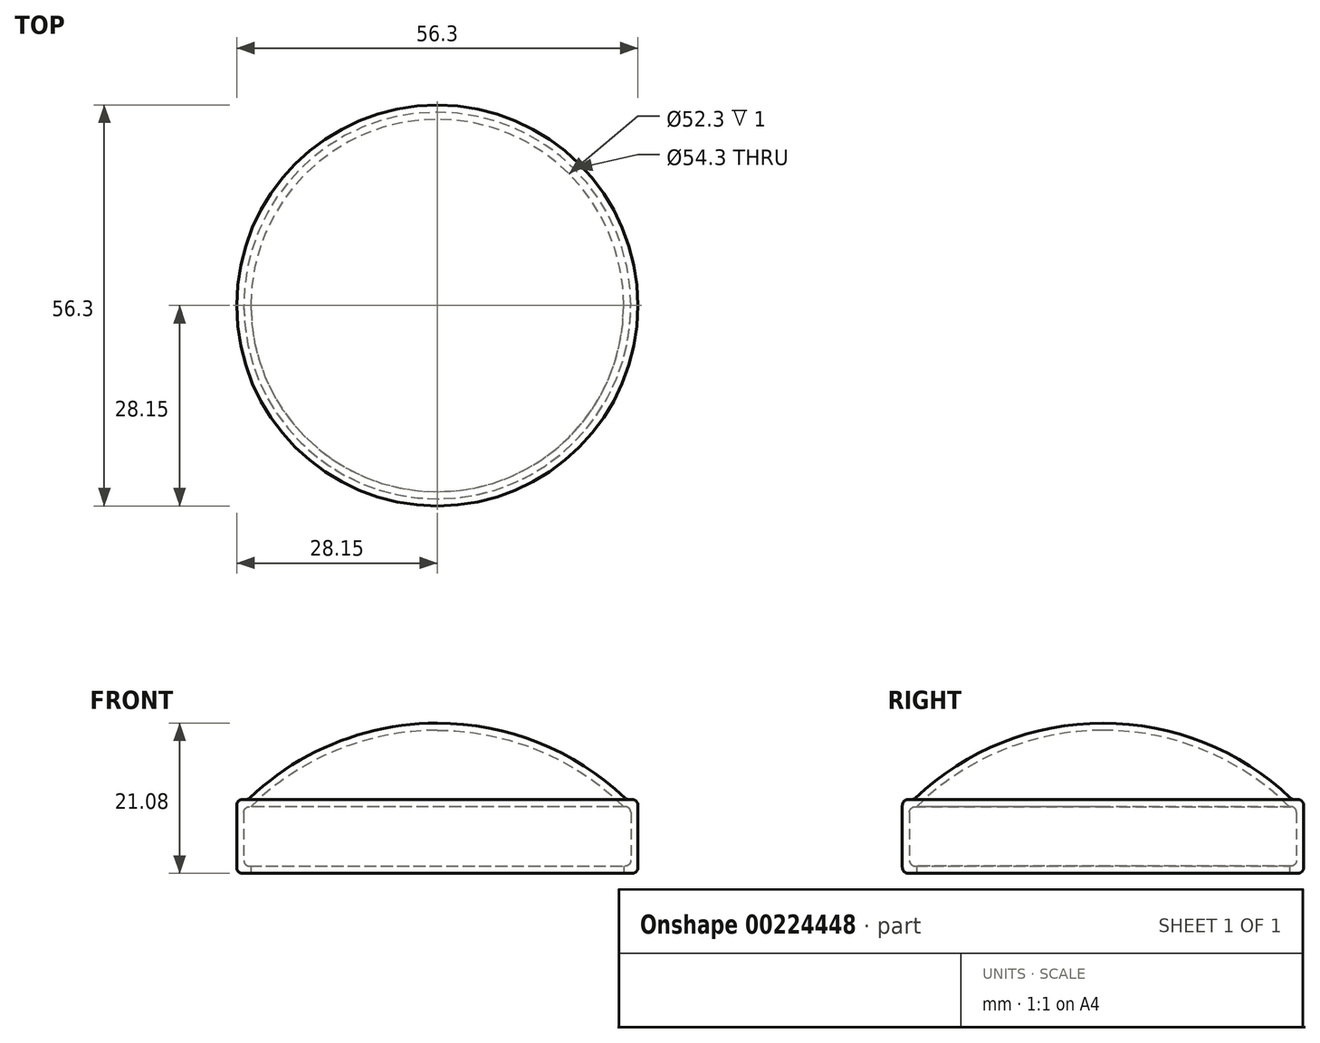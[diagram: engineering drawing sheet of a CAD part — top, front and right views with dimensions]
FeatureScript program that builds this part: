
annotation { "Feature Type Name" : "Feature", "Feature Type Description" : "" }
export const myFeature = defineFeature(function(context is Context, id is Id, definition is map)
    precondition{}
    {
        {
            assignVariable(context, id + "F0", {"name" : "WallThickness", "anyValue" : 1});
        }
        {
            var Q0;
            Q0=qCreatedBy(makeId("Front.planeOp"),FACE);
            var sketch = newSketch(context, id + "F1", { "sketchPlane" : qUnion([Q0])});
            skLineSegment(sketch, "E0", {"start": v(0, 0) * mm, "end": v(0, 27.56) * mm});
            skLineSegment(sketch, "E1", {"start": v(-26.15, 0) * mm, "end": v(-28.15, 0) * mm});
            skLineSegment(sketch, "E2", {"start": v(-28.15, 0) * mm, "end": v(-28.15, 10.35) * mm});
            skLineSegment(sketch, "E3", {"start": v(-28.15, 10.35) * mm, "end": v(-26.56, 10.35) * mm});
            skLineSegment(sketch, "E4", {"start": v(-26.15, 1) * mm, "end": v(-27.15, 1) * mm});
            skLineSegment(sketch, "E5", {"start": v(-27.15, 1) * mm, "end": v(-27.15, 9.35) * mm});
            skLineSegment(sketch, "E6", {"start": v(-27.15, 9.35) * mm, "end": v(-26.15, 9.35) * mm});
            skLineSegment(sketch, "E7", {"start": v(-26.15, 0) * mm, "end": v(-26.15, 1) * mm});
            skArc(sketch, "E8", {"start": v(0, 21.08) * mm, "mid": v(-14.32, 18.3) * mm, "end": v(-26.56, 10.35) * mm});
            skArc(sketch, "E9.0", {"start": v(0, 20.08) * mm, "mid": v(-14.13, 17.3) * mm, "end": v(-26.15, 9.35) * mm});
            skSolve(sketch);
        }
        {
            var Q0;
            Q0=makeQuery(id+"F1.imprint","IMPRINT",FACE,{"disambiguationData":[TD([[makeQuery(id+"F1.imprint","IMPRINT",EDGE,{"derivedFrom":sQuery(id+"F1.wireOp",EDGE,"E1")}),-1.0]])]});
            var Q1;
            Q1=sQuery(id+"F1.wireOp",EDGE,"E0");
            revolve(context, id + "F2", {"entities" : qUnion([Q0]), "axis" : qUnion([Q1]), "revolveType" : RevolveType.FULL});
        }
        {
            var Q0;
            Q0=makeQuery(id+"F2.opRevolve","SWEPT_FACE",FACE,{"disambiguationData":[OSD([sQuery(id+"F1.wireOp",EDGE,"E2")])]});
            var Q1;
            Q1=makeQuery(id+"F2.opRevolve","SWEPT_FACE",FACE,{"disambiguationData":[OSD([sQuery(id+"F1.wireOp",EDGE,"E8")])]});
            var Q2;
            Q2=makeQuery(id+"F2.opRevolve","SWEPT_FACE",FACE,{"disambiguationData":[OSD([sQuery(id+"F1.wireOp",EDGE,"E5")])]});
            fillet(context, id + "F3", {"entities" : qUnion([Q0, Q1, Q2]), "radius" : (getVariable(context, 'WallThickness') - .2) * mm, "tangentPropagation" : true, "allowEdgeOverflow" : false});
        }
    });
